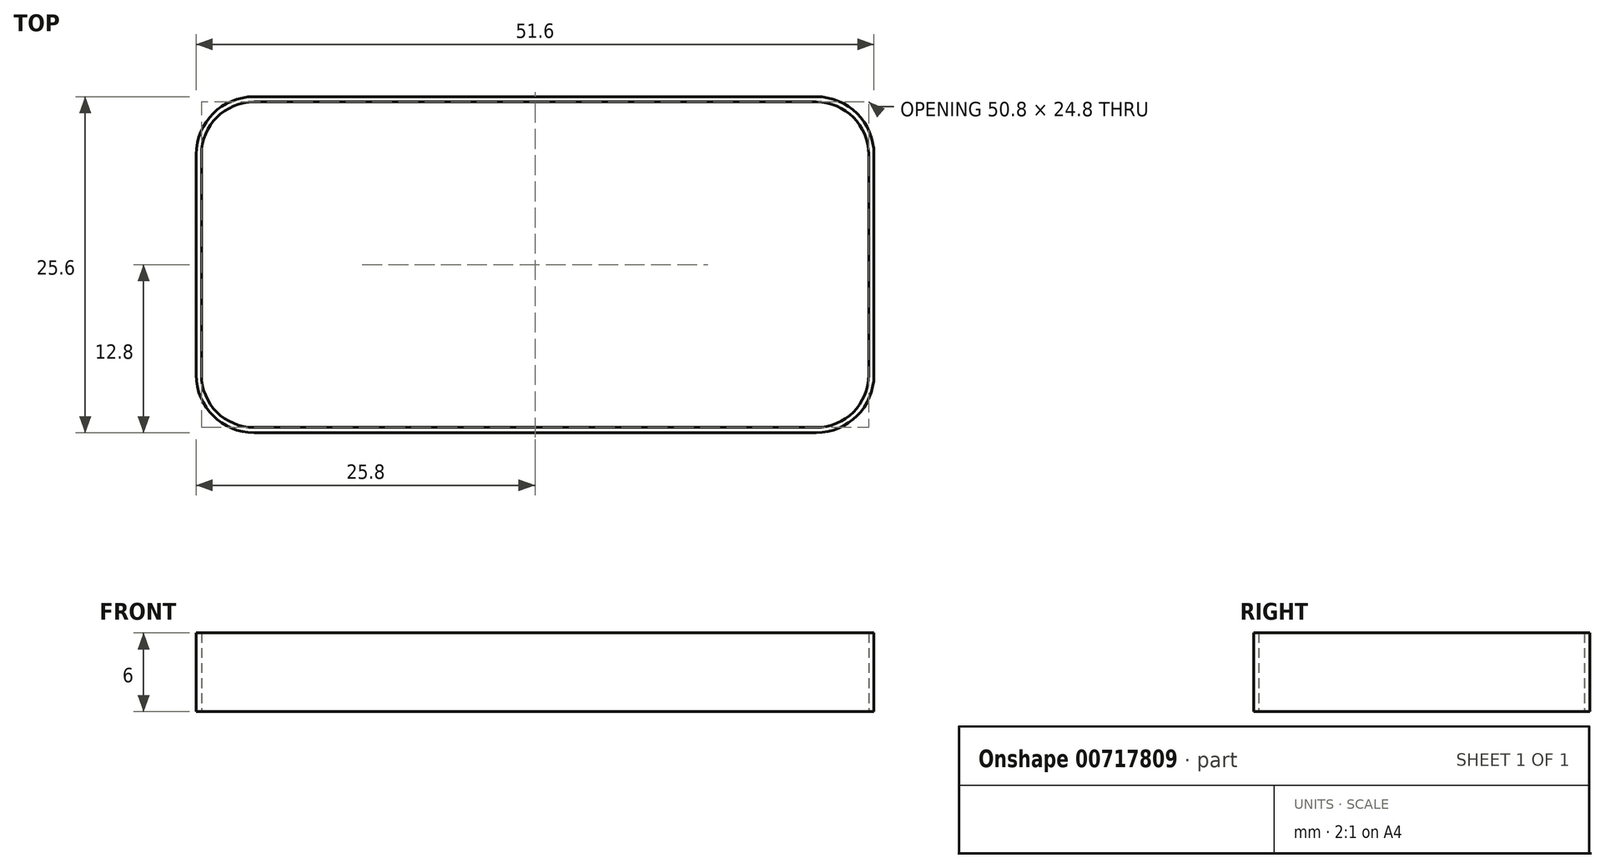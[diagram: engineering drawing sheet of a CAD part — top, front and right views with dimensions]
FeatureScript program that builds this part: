
annotation { "Feature Type Name" : "Feature", "Feature Type Description" : "" }
export const myFeature = defineFeature(function(context is Context, id is Id, definition is map)
    precondition{}
    {
        {
            var Q0;
            Q0=qCreatedBy(makeId("Top.planeOp"),FACE);
            var sketch = newSketch(context, id + "F0", { "sketchPlane" : qUnion([Q0])});
            skLineSegment(sketch, "E0.bottom", {"start": v(25.8, -12.8) * mm, "end": v(-25.8, -12.8) * mm});
            skLineSegment(sketch, "E0.top", {"start": v(25.8, 12.8) * mm, "end": v(-25.8, 12.8) * mm});
            skLineSegment(sketch, "E0.left", {"start": v(25.8, -12.8) * mm, "end": v(25.8, 12.8) * mm});
            skLineSegment(sketch, "E0.right", {"start": v(-25.8, -12.8) * mm, "end": v(-25.8, 12.8) * mm});
            skPoint(sketch, "E0.middle", {"position": v(0, 0) * mm});
            skLineSegment(sketch, "E1.bottom", {"start": v(-25.4, 12.4) * mm, "end": v(25.4, 12.4) * mm});
            skLineSegment(sketch, "E1.top", {"start": v(-25.4, -12.4) * mm, "end": v(25.4, -12.4) * mm});
            skLineSegment(sketch, "E1.left", {"start": v(-25.4, 12.4) * mm, "end": v(-25.4, -12.4) * mm});
            skLineSegment(sketch, "E1.right", {"start": v(25.4, 12.4) * mm, "end": v(25.4, -12.4) * mm});
            skSolve(sketch);
        }
        {
            var Q0;
            Q0=makeQuery(id+"F0.imprint","IMPRINT",FACE,{"disambiguationData":[TD([[makeQuery(id+"F0.imprint","IMPRINT",EDGE,{"derivedFrom":sQuery(id+"F0.wireOp",EDGE,"E0.bottom")}),-1.0]])]});
            extrude(context, id + "F1", {"entities" : qUnion([Q0]), "depth" : 6 * mm, "offsetDistance" : 25 * mm});
        }
        {
            var Q0;
            Q0=makeQuery(id+"F1.opExtrude","SWEPT_EDGE",EDGE,{"disambiguationData":[OSD([sQuery(id+"F0.wireOp",EDGE,"E1.bottom"),sQuery(id+"F0.wireOp",EDGE,"E1.left")])]});
            var Q1;
            Q1=makeQuery(id+"F1.opExtrude","SWEPT_EDGE",EDGE,{"disambiguationData":[OSD([sQuery(id+"F0.wireOp",EDGE,"E1.bottom"),sQuery(id+"F0.wireOp",EDGE,"E1.right")])]});
            var Q2;
            Q2=makeQuery(id+"F1.opExtrude","SWEPT_EDGE",EDGE,{"disambiguationData":[OSD([sQuery(id+"F0.wireOp",EDGE,"E1.top"),sQuery(id+"F0.wireOp",EDGE,"E1.right")])]});
            var Q3;
            Q3=makeQuery(id+"F1.opExtrude","SWEPT_EDGE",EDGE,{"disambiguationData":[OSD([sQuery(id+"F0.wireOp",EDGE,"E1.top"),sQuery(id+"F0.wireOp",EDGE,"E1.left")])]});
            fillet(context, id + "F2", {"entities" : qUnion([Q0, Q1, Q2, Q3]), "radius" : 4 * mm, "tangentPropagation" : true, "allowEdgeOverflow" : false});
        }
        {
            var Q0;
            Q0=makeQuery(id+"F1.opExtrude","SWEPT_EDGE",EDGE,{"disambiguationData":[OSD([sQuery(id+"F0.wireOp",EDGE,"E0.top"),sQuery(id+"F0.wireOp",EDGE,"E0.left")])]});
            var Q1;
            Q1=makeQuery(id+"F1.opExtrude","SWEPT_EDGE",EDGE,{"disambiguationData":[OSD([sQuery(id+"F0.wireOp",EDGE,"E0.bottom"),sQuery(id+"F0.wireOp",EDGE,"E0.left")])]});
            var Q2;
            Q2=makeQuery(id+"F1.opExtrude","SWEPT_EDGE",EDGE,{"disambiguationData":[OSD([sQuery(id+"F0.wireOp",EDGE,"E0.bottom"),sQuery(id+"F0.wireOp",EDGE,"E0.right")])]});
            var Q3;
            Q3=makeQuery(id+"F1.opExtrude","SWEPT_EDGE",EDGE,{"disambiguationData":[OSD([sQuery(id+"F0.wireOp",EDGE,"E0.top"),sQuery(id+"F0.wireOp",EDGE,"E0.right")])]});
            fillet(context, id + "F3", {"entities" : qUnion([Q0, Q1, Q2, Q3]), "radius" : 4.4 * mm, "tangentPropagation" : true, "allowEdgeOverflow" : false});
        }
    });
